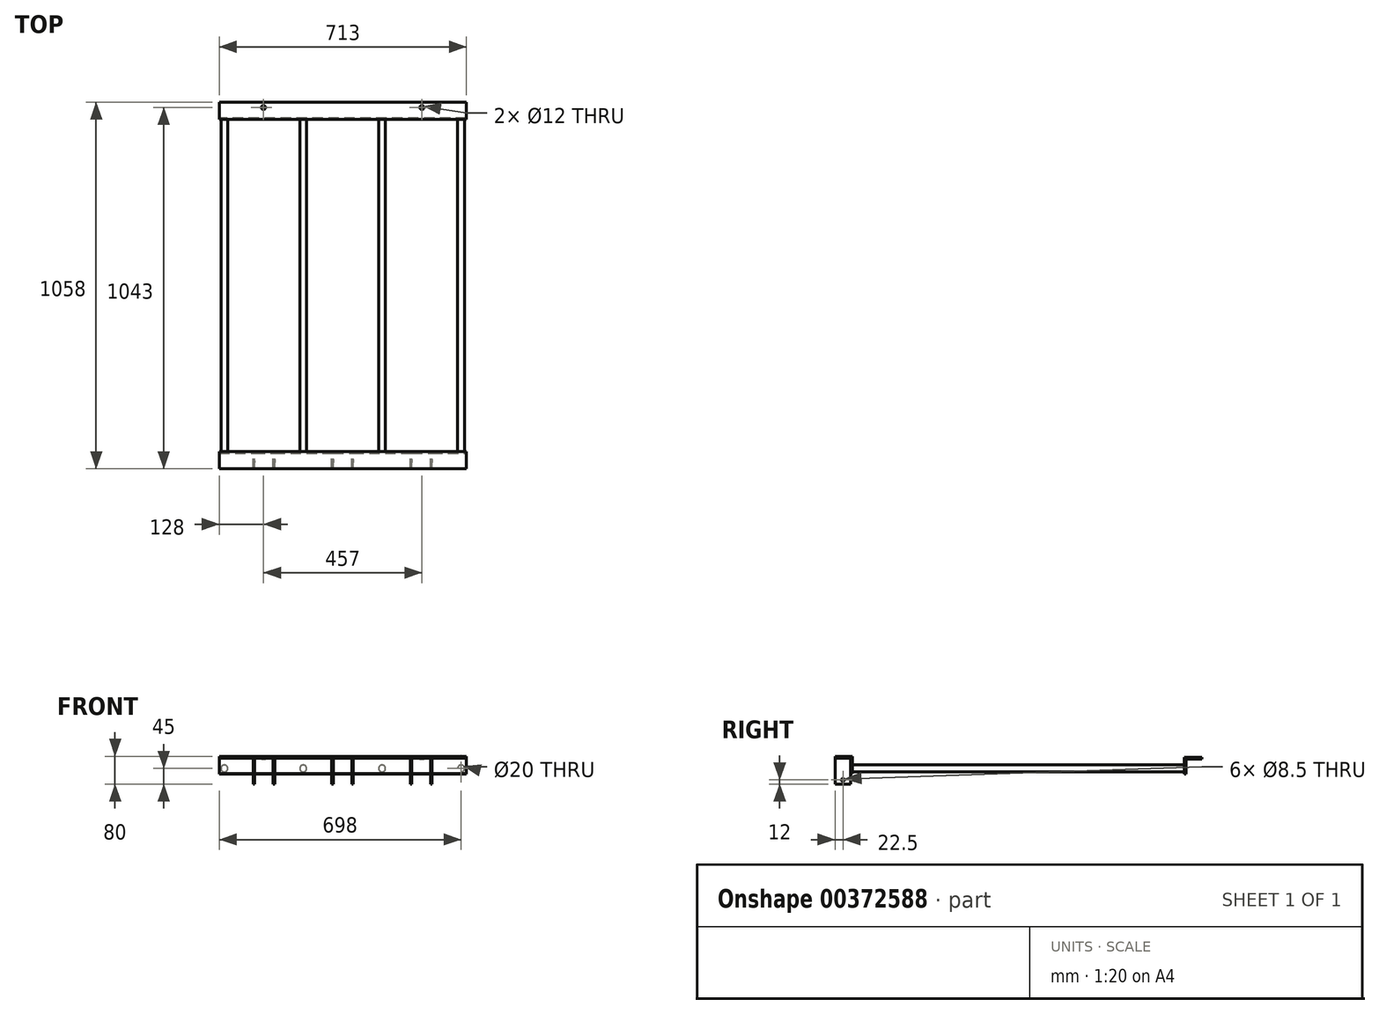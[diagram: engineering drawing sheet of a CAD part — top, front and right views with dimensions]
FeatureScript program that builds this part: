
annotation { "Feature Type Name" : "Feature", "Feature Type Description" : "" }
export const myFeature = defineFeature(function(context is Context, id is Id, definition is map)
    precondition{}
    {
        {
            var Q0;
            Q0=qCreatedBy(makeId("Right.planeOp"),FACE);
            var sketch = newSketch(context, id + "F0", { "sketchPlane" : qUnion([Q0])});
            skLineSegment(sketch, "E0", {"start": v(-32.53, 45) * mm, "end": v(17.47, 45) * mm});
            skLineSegment(sketch, "E1", {"start": v(17.47, 45) * mm, "end": v(17.47, -5) * mm});
            skLineSegment(sketch, "E2", {"start": v(17.47, -5) * mm, "end": v(12.47, -5) * mm});
            skLineSegment(sketch, "E3", {"start": v(12.47, -5) * mm, "end": v(12.47, 40) * mm});
            skLineSegment(sketch, "E4", {"start": v(12.47, 40) * mm, "end": v(-32.53, 40) * mm});
            skLineSegment(sketch, "E5", {"start": v(-32.53, 40) * mm, "end": v(-32.53, 45) * mm});
            skLineSegment(sketch, "E6", {"start": v(597.9, -5) * mm, "end": v(597.9, 42) * mm});
            skLineSegment(sketch, "E7", {"start": v(597.9, 42) * mm, "end": v(602.9, 42) * mm});
            skLineSegment(sketch, "E8", {"start": v(602.9, 42) * mm, "end": v(602.9, 0) * mm});
            skLineSegment(sketch, "E9", {"start": v(602.9, 0) * mm, "end": v(644.9, 0) * mm});
            skLineSegment(sketch, "E10", {"start": v(644.9, 0) * mm, "end": v(644.9, -5) * mm});
            skLineSegment(sketch, "E11", {"start": v(644.9, -5) * mm, "end": v(597.9, -5) * mm});
            skSolve(sketch);
        }
        {
            var Q0;
            Q0=makeQuery(id+"F0.imprint","IMPRINT",FACE,{"disambiguationData":[TD([[makeQuery(id+"F0.imprint","IMPRINT",EDGE,{"derivedFrom":sQuery(id+"F0.wireOp",EDGE,"E0")}),-1.0]])]});
            extrude(context, id + "F1", {"entities" : qUnion([Q0]), "oppositeDirection" : true, "depth" : 713 * mm});
        }
        {
            var Q0;
            Q0=makeQuery(id+"F1.opExtrude","SWEPT_FACE",FACE,{"disambiguationData":[OSD([sQuery(id+"F0.wireOp",EDGE,"E1")])]});
            var sketch = newSketch(context, id + "F2", { "sketchPlane" : qUnion([Q0])});
            skCircle(sketch, "E12", {"center": v(15, 10) * mm, "radius": 10 * mm});
            skCircle(sketch, "E13", {"center": v(243, 10) * mm, "radius": 10 * mm});
            skCircle(sketch, "E14", {"center": v(470.5, 10) * mm, "radius": 10 * mm});
            skCircle(sketch, "E15", {"center": v(698, 10) * mm, "radius": 10 * mm});
            skSolve(sketch);
        }
        {
            var Q0;
            Q0=makeQuery(id+"F2.imprint","IMPRINT",FACE,{"disambiguationData":[TD([[makeQuery(id+"F2.imprint","IMPRINT",EDGE,{"derivedFrom":sQuery(id+"F2.wireOp",EDGE,"E15")}),1.0]])]});
            var Q1;
            Q1=makeQuery(id+"F2.imprint","IMPRINT",FACE,{"disambiguationData":[TD([[makeQuery(id+"F2.imprint","IMPRINT",EDGE,{"derivedFrom":sQuery(id+"F2.wireOp",EDGE,"E14")}),1.0]])]});
            var Q2;
            Q2=makeQuery(id+"F2.imprint","IMPRINT",FACE,{"disambiguationData":[TD([[makeQuery(id+"F2.imprint","IMPRINT",EDGE,{"derivedFrom":sQuery(id+"F2.wireOp",EDGE,"E13")}),1.0]])]});
            var Q3;
            Q3=makeQuery(id+"F2.imprint","IMPRINT",FACE,{"disambiguationData":[TD([[makeQuery(id+"F2.imprint","IMPRINT",EDGE,{"derivedFrom":sQuery(id+"F2.wireOp",EDGE,"E12")}),1.0]])]});
            extrude(context, id + "F3", {"entities" : qUnion([Q0, Q1, Q2, Q3]), "operationType" : NewBodyOperationType.ADD, "depth" : 958 * mm});
        }
        {
            var Q0;
            Q0=makeQuery(id+"F3.opExtrude","CAP_FACE",FACE,{"disambiguationData":[OSD([sQuery(id+"F2.wireOp",EDGE,"E12")])],"isStart":false});
            var sketch = newSketch(context, id + "F4", { "sketchPlane" : qUnion([Q0])});
            skLineSegment(sketch, "E16.bottom", {"start": v(0, 41.77) * mm, "end": v(0, 41.77) * mm});
            skLineSegment(sketch, "E16.top", {"start": v(0, -6.95) * mm, "end": v(0, -6.95) * mm});
            skLineSegment(sketch, "E16.left", {"start": v(0, 41.77) * mm, "end": v(0, -6.95) * mm});
            skLineSegment(sketch, "E16.right", {"start": v(0, 41.77) * mm, "end": v(0, -6.95) * mm});
            skLineSegment(sketch, "E17.bottom", {"start": v(0, 41.77) * mm, "end": v(713, 41.77) * mm});
            skLineSegment(sketch, "E17.top", {"start": v(0, -5.53) * mm, "end": v(713, -5.53) * mm});
            skLineSegment(sketch, "E17.left", {"start": v(0, 41.77) * mm, "end": v(0, -5.53) * mm});
            skLineSegment(sketch, "E17.right", {"start": v(713, 41.77) * mm, "end": v(713, -5.53) * mm});
            skSolve(sketch);
        }
        {
            var Q0;
            Q0=makeQuery(id+"F4.imprint","IMPRINT",FACE,{"disambiguationData":[TD([[makeQuery(id+"F4.imprint","IMPRINT",EDGE,{"derivedFrom":sQuery(id+"F4.wireOp",EDGE,"E17.bottom")}),-1.0]])]});
            extrude(context, id + "F5", {"entities" : qUnion([Q0]), "depth" : 5 * mm});
        }
        {
            var Q0;
            Q0=makeQuery(id+"F5.opExtrude","CAP_FACE",FACE,{"disambiguationData":[OSD([sQuery(id+"F2.wireOp",EDGE,"E12"),sQuery(id+"F4.wireOp",EDGE,"E17.bottom"),sQuery(id+"F4.wireOp",EDGE,"E17.top"),sQuery(id+"F4.wireOp",EDGE,"E17.left"),sQuery(id+"F4.wireOp",EDGE,"E17.right")])],"isStart":false});
            var sketch = newSketch(context, id + "F6", { "sketchPlane" : qUnion([Q0])});
            skLineSegment(sketch, "E18.bottom", {"start": v(0, 41.77) * mm, "end": v(713, 41.77) * mm});
            skLineSegment(sketch, "E18.top", {"start": v(0, 36.77) * mm, "end": v(713, 36.77) * mm});
            skLineSegment(sketch, "E18.left", {"start": v(0, 41.77) * mm, "end": v(0, 36.77) * mm});
            skLineSegment(sketch, "E18.right", {"start": v(713, 41.77) * mm, "end": v(713, 36.77) * mm});
            skSolve(sketch);
        }
        {
            var Q0;
            Q0=makeQuery(id+"F6.imprint","IMPRINT",FACE,{"disambiguationData":[TD([[makeQuery(id+"F6.imprint","IMPRINT",EDGE,{"derivedFrom":sQuery(id+"F6.wireOp",EDGE,"E18.bottom")}),-1.0]])]});
            extrude(context, id + "F7", {"entities" : qUnion([Q0]), "operationType" : NewBodyOperationType.ADD, "depth" : 45 * mm});
        }
        {
            var Q0;
            Q0=makeQuery(id+"F7.opExtrude","CAP_FACE",FACE,{"disambiguationData":[OSD([sQuery(id+"F6.wireOp",EDGE,"E18.bottom"),sQuery(id+"F6.wireOp",EDGE,"E18.top"),sQuery(id+"F6.wireOp",EDGE,"E18.left"),sQuery(id+"F6.wireOp",EDGE,"E18.right")])],"isStart":false});
            var sketch = newSketch(context, id + "F8", { "sketchPlane" : qUnion([Q0])});
            skLineSegment(sketch, "E19.bottom", {"start": v(98, 41.77) * mm, "end": v(158, 41.77) * mm});
            skLineSegment(sketch, "E19.top", {"start": v(98, 36.77) * mm, "end": v(158, 36.77) * mm});
            skLineSegment(sketch, "E19.left", {"start": v(98, 41.77) * mm, "end": v(98, 36.77) * mm});
            skLineSegment(sketch, "E19.right", {"start": v(158, 41.77) * mm, "end": v(158, 36.77) * mm});
            skLineSegment(sketch, "E20.bottom", {"start": v(326, 41.77) * mm, "end": v(386, 41.77) * mm});
            skLineSegment(sketch, "E20.top", {"start": v(326, 36.77) * mm, "end": v(386, 36.77) * mm});
            skLineSegment(sketch, "E20.left", {"start": v(326, 41.77) * mm, "end": v(326, 36.77) * mm});
            skLineSegment(sketch, "E20.right", {"start": v(386, 41.77) * mm, "end": v(386, 36.77) * mm});
            skLineSegment(sketch, "E21.bottom", {"start": v(554, 41.77) * mm, "end": v(614, 41.77) * mm});
            skLineSegment(sketch, "E21.top", {"start": v(554, 36.77) * mm, "end": v(614, 36.77) * mm});
            skLineSegment(sketch, "E21.left", {"start": v(554, 41.77) * mm, "end": v(554, 36.77) * mm});
            skLineSegment(sketch, "E21.right", {"start": v(614, 41.77) * mm, "end": v(614, 36.77) * mm});
            skSolve(sketch);
        }
        {
            var Q0;
            Q0=makeQuery(id+"F9SSsXqYL4VzCJi_2.boolean.opBoolean","MERGE",FACE,{"derivedFrom":[makeQuery(id+"F7.boolean.opBoolean","MERGE",FACE,{"derivedFrom":[makeQuery(id+"F5.opExtrude","SWEPT_FACE",FACE,{"disambiguationData":[OSD([sQuery(id+"F4.wireOp",EDGE,"E17.bottom")])]}),makeQuery(id+"F7.opExtrude","SWEPT_FACE",FACE,{"disambiguationData":[OSD([sQuery(id+"F6.wireOp",EDGE,"E18.bottom")])]})]}),makeQuery(id+"F9SSsXqYL4VzCJi_2.opExtrude","SWEPT_FACE",FACE,{"disambiguationData":[OSD([sQuery(id+"F8.wireOp",EDGE,"E19.bottom")])]}),makeQuery(id+"F9SSsXqYL4VzCJi_2.opExtrude","SWEPT_FACE",FACE,{"disambiguationData":[OSD([sQuery(id+"F8.wireOp",EDGE,"E20.bottom")])]}),makeQuery(id+"F9SSsXqYL4VzCJi_2.opExtrude","SWEPT_FACE",FACE,{"disambiguationData":[OSD([sQuery(id+"F8.wireOp",EDGE,"E21.bottom")])]})]});
            var sketch = newSketch(context, id + "F9", { "sketchPlane" : qUnion([Q0])});
            skCircle(sketch, "E22", {"center": v(-129, 1013.47) * mm, "radius": 6 * mm});
            skCircle(sketch, "E23", {"center": v(-584, 1013.47) * mm, "radius": 6 * mm});
            skSolve(sketch);
        }
        {
            var Q0;
            Q0=makeQuery(id+"F1.opExtrude","SWEPT_FACE",FACE,{"disambiguationData":[OSD([sQuery(id+"F0.wireOp",EDGE,"E4")])]});
            var sketch = newSketch(context, id + "F10", { "sketchPlane" : qUnion([Q0])});
            skLineSegment(sketch, "E24.bottom", {"start": v(-615, 32.53) * mm, "end": v(-611, 32.53) * mm});
            skLineSegment(sketch, "E24.top", {"start": v(-615, -12.47) * mm, "end": v(-611, -12.47) * mm});
            skLineSegment(sketch, "E24.left", {"start": v(-615, 32.53) * mm, "end": v(-615, -12.47) * mm});
            skLineSegment(sketch, "E24.right", {"start": v(-611, 32.53) * mm, "end": v(-611, -12.47) * mm});
            skLineSegment(sketch, "E25.bottom", {"start": v(-557, 32.53) * mm, "end": v(-553, 32.53) * mm});
            skLineSegment(sketch, "E25.top", {"start": v(-557, -12.47) * mm, "end": v(-553, -12.47) * mm});
            skLineSegment(sketch, "E25.left", {"start": v(-557, 32.53) * mm, "end": v(-557, -12.47) * mm});
            skLineSegment(sketch, "E25.right", {"start": v(-553, 32.53) * mm, "end": v(-553, -12.47) * mm});
            skLineSegment(sketch, "E26.bottom", {"start": v(-388, 32.53) * mm, "end": v(-384, 32.53) * mm});
            skLineSegment(sketch, "E26.top", {"start": v(-388, -12.47) * mm, "end": v(-384, -12.47) * mm});
            skLineSegment(sketch, "E26.left", {"start": v(-388, 32.53) * mm, "end": v(-388, -12.47) * mm});
            skLineSegment(sketch, "E26.right", {"start": v(-384, 32.53) * mm, "end": v(-384, -12.47) * mm});
            skLineSegment(sketch, "E27.bottom", {"start": v(-330, 32.53) * mm, "end": v(-326, 32.53) * mm});
            skLineSegment(sketch, "E27.top", {"start": v(-330, -12.47) * mm, "end": v(-326, -12.47) * mm});
            skLineSegment(sketch, "E27.left", {"start": v(-330, 32.53) * mm, "end": v(-330, -12.47) * mm});
            skLineSegment(sketch, "E27.right", {"start": v(-326, 32.53) * mm, "end": v(-326, -12.47) * mm});
            skLineSegment(sketch, "E28.bottom", {"start": v(-157, 32.53) * mm, "end": v(-161, 32.53) * mm});
            skLineSegment(sketch, "E28.top", {"start": v(-157, -12.47) * mm, "end": v(-161, -12.47) * mm});
            skLineSegment(sketch, "E28.left", {"start": v(-157, 32.53) * mm, "end": v(-157, -12.47) * mm});
            skLineSegment(sketch, "E28.right", {"start": v(-161, 32.53) * mm, "end": v(-161, -12.47) * mm});
            skLineSegment(sketch, "E29.bottom", {"start": v(-103, 32.53) * mm, "end": v(-99, 32.53) * mm});
            skLineSegment(sketch, "E29.top", {"start": v(-103, -12.47) * mm, "end": v(-99, -12.47) * mm});
            skLineSegment(sketch, "E29.left", {"start": v(-103, 32.53) * mm, "end": v(-103, -12.47) * mm});
            skLineSegment(sketch, "E29.right", {"start": v(-99, 32.53) * mm, "end": v(-99, -12.47) * mm});
            skSolve(sketch);
        }
        {
            var Q0;
            Q0=makeQuery(id+"F10.imprint","IMPRINT",FACE,{"disambiguationData":[TD([[makeQuery(id+"F10.imprint","IMPRINT",EDGE,{"derivedFrom":sQuery(id+"F10.wireOp",EDGE,"E24.bottom")}),-1.0]])]});
            var Q1;
            Q1=makeQuery(id+"F10.imprint","IMPRINT",FACE,{"disambiguationData":[TD([[makeQuery(id+"F10.imprint","IMPRINT",EDGE,{"derivedFrom":sQuery(id+"F10.wireOp",EDGE,"E25.bottom")}),-1.0]])]});
            var Q2;
            Q2=makeQuery(id+"F10.imprint","IMPRINT",FACE,{"disambiguationData":[TD([[makeQuery(id+"F10.imprint","IMPRINT",EDGE,{"derivedFrom":sQuery(id+"F10.wireOp",EDGE,"E26.bottom")}),-1.0]])]});
            var Q3;
            Q3=makeQuery(id+"F10.imprint","IMPRINT",FACE,{"disambiguationData":[TD([[makeQuery(id+"F10.imprint","IMPRINT",EDGE,{"derivedFrom":sQuery(id+"F10.wireOp",EDGE,"E27.bottom")}),-1.0]])]});
            var Q4;
            Q4=makeQuery(id+"F10.imprint","IMPRINT",FACE,{"disambiguationData":[TD([[makeQuery(id+"F10.imprint","IMPRINT",EDGE,{"derivedFrom":sQuery(id+"F10.wireOp",EDGE,"E28.bottom")}),-1.0]])]});
            var Q5;
            Q5=makeQuery(id+"F10.imprint","IMPRINT",FACE,{"disambiguationData":[TD([[makeQuery(id+"F10.imprint","IMPRINT",EDGE,{"derivedFrom":sQuery(id+"F10.wireOp",EDGE,"E29.bottom")}),-1.0]])]});
            extrude(context, id + "F11", {"entities" : qUnion([Q0, Q1, Q2, Q3, Q4, Q5]), "operationType" : NewBodyOperationType.ADD, "depth" : 75 * mm});
        }
        {
            var Q0;
            Q0=makeQuery(id+"F11.opExtrude","SWEPT_FACE",FACE,{"disambiguationData":[OSD([sQuery(id+"F10.wireOp",EDGE,"E24.left")])]});
            var sketch = newSketch(context, id + "F12", { "sketchPlane" : qUnion([Q0])});
            skCircle(sketch, "E30", {"center": v(10.03, -23) * mm, "radius": 4.5 * mm});
            skSolve(sketch);
        }
        {
            var Q0;
            Q0=sQuery(id+"F12.wireOp",VERTEX,"E30.center");
            var Q1;
            Q1=makeQuery(id+"F1.opExtrude","SWEPT_BODY",BODY,{"disambiguationData":[OSD([sQuery(id+"F0.wireOp",EDGE,"E0"),sQuery(id+"F0.wireOp",EDGE,"E1"),sQuery(id+"F0.wireOp",EDGE,"E2"),sQuery(id+"F0.wireOp",EDGE,"E3"),sQuery(id+"F0.wireOp",EDGE,"E4"),sQuery(id+"F0.wireOp",EDGE,"E5")])]});
            hole(context, id + "F13", {"style" : HoleStyle.SIMPLE, "endStyle" : HoleEndStyle.THROUGH, "holeDiameter" : 8.5 * mm, "isTappedThrough" : true, "tappedDepth" : 12 * mm, "tapClearance" : 3, "locations" : qUnion([Q0]), "scope" : qUnion([Q1])});
        }
        {
            var Q0;
            Q0=makeQuery(id+"F9.imprint","IMPRINT",FACE,{"disambiguationData":[TD([[makeQuery(id+"F9.imprint","IMPRINT",EDGE,{"derivedFrom":sQuery(id+"F9.wireOp",EDGE,"E22")}),-1.0]])]});
            var sketch = newSketch(context, id + "F14", { "sketchPlane" : qUnion([Q0])});
            skCircle(sketch, "E31", {"center": v(-585, 1010.47) * mm, "radius": 4.5 * mm});
            skCircle(sketch, "E32", {"center": v(-128, 1010.47) * mm, "radius": 4.5 * mm});
            skSolve(sketch);
        }
        {
            var Q0;
            Q0=sQuery(id+"F14.wireOp",VERTEX,"E31.center");
            var Q1;
            Q1=sQuery(id+"F14.wireOp",VERTEX,"E32.center");
            var Q2;
            Q2=makeQuery(id+"F5.opExtrude","SWEPT_BODY",BODY,{"disambiguationData":[OSD([sQuery(id+"F2.wireOp",EDGE,"E12"),sQuery(id+"F4.wireOp",EDGE,"E17.bottom"),sQuery(id+"F4.wireOp",EDGE,"E17.top"),sQuery(id+"F4.wireOp",EDGE,"E17.left"),sQuery(id+"F4.wireOp",EDGE,"E17.right")])]});
            hole(context, id + "F15", {"style" : HoleStyle.SIMPLE, "endStyle" : HoleEndStyle.THROUGH, "holeDiameter" : 12 * mm, "isTappedThrough" : true, "tappedDepth" : 12 * mm, "tapClearance" : 3, "locations" : qUnion([Q0, Q1]), "scope" : qUnion([Q2])});
        }
        {
            var Q0;
            Q0=makeQuery(id+"F11.boolean.opBoolean","MERGE",FACE,{"derivedFrom":[makeQuery(id+"F1.opExtrude","SWEPT_FACE",FACE,{"disambiguationData":[OSD([sQuery(id+"F0.wireOp",EDGE,"E5")])]}),makeQuery(id+"F11.opExtrude","SWEPT_FACE",FACE,{"disambiguationData":[OSD([sQuery(id+"F10.wireOp",EDGE,"E24.bottom")])]}),makeQuery(id+"F11.opExtrude","SWEPT_FACE",FACE,{"disambiguationData":[OSD([sQuery(id+"F10.wireOp",EDGE,"E25.bottom")])]}),makeQuery(id+"F11.opExtrude","SWEPT_FACE",FACE,{"disambiguationData":[OSD([sQuery(id+"F10.wireOp",EDGE,"E26.bottom")])]}),makeQuery(id+"F11.opExtrude","SWEPT_FACE",FACE,{"disambiguationData":[OSD([sQuery(id+"F10.wireOp",EDGE,"E27.bottom")])]}),makeQuery(id+"F11.opExtrude","SWEPT_FACE",FACE,{"disambiguationData":[OSD([sQuery(id+"F10.wireOp",EDGE,"E28.bottom")])]}),makeQuery(id+"F11.opExtrude","SWEPT_FACE",FACE,{"disambiguationData":[OSD([sQuery(id+"F10.wireOp",EDGE,"E29.bottom")])]})]});
            cPlane(context, id + "F16", {"entities" : qUnion([Q0]), "cplaneType" : CPlaneType.OFFSET, "offset" : 22.5 * mm, "oppositeDirection" : true, "width" : 150 * mm, "height" : 150 * mm});
        }
    });
